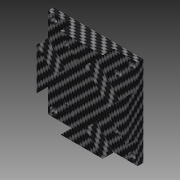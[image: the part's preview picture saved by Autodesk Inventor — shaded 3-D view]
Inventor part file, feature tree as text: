
AUTODESK INVENTOR PART (.ipt)
format: ipt  version: 2015 (Build 190159000, 159)  size: 137,216 bytes
history: native  units: mm
features: extrude x2, sketch x1
ambient origin geometry x8: Origin, YZ Plane, XZ Plane, XY Plane, X Axis, Y Axis, Z Axis, Center Point
bodies: Solid1 (feature_tree)
feature tree (3):
  sketch  "Sketch1"  dims[d8=4.0mm d10=2.5mm d11=2.5mm d43=6.0mm d44=0.0mm d45=4.0mm d46=0.0mm]
  extrude  "Extrusion1"  Depth=4.0mm
  extrude  "Extrusion2"  Depth=4.0mm
